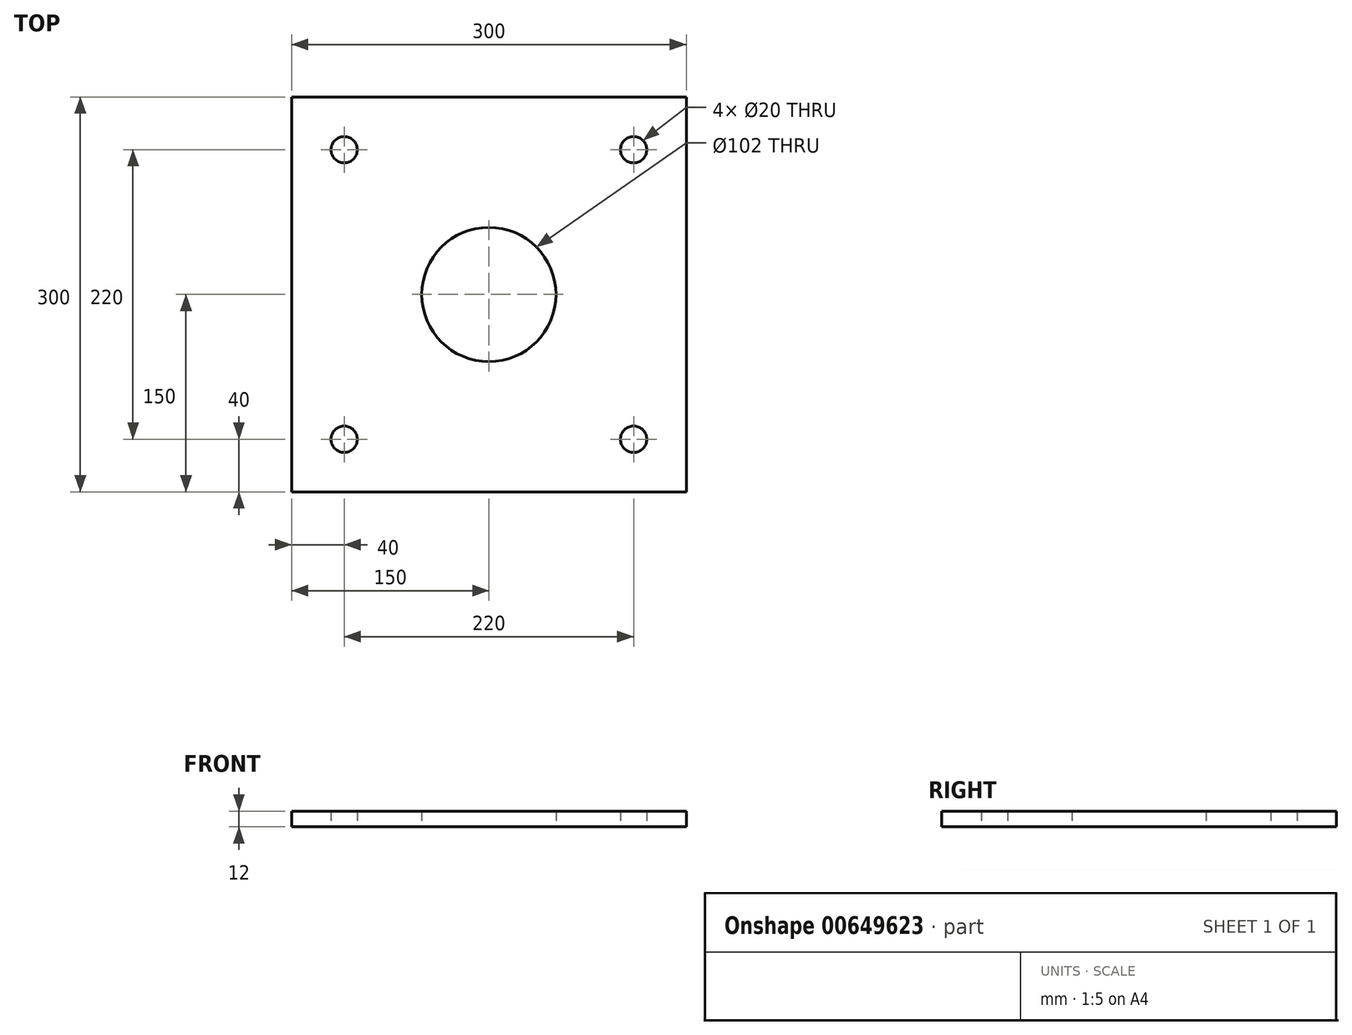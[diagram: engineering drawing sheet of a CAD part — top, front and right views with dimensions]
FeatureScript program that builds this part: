
annotation { "Feature Type Name" : "Feature", "Feature Type Description" : "" }
export const myFeature = defineFeature(function(context is Context, id is Id, definition is map)
    precondition{}
    {
        {
            var Q0;
            Q0=qCreatedBy(makeId("Top.planeOp"),FACE);
            var sketch = newSketch(context, id + "F0", { "sketchPlane" : qUnion([Q0])});
            skLineSegment(sketch, "E0.bottom", {"start": v(150, -150) * mm, "end": v(-150, -150) * mm});
            skLineSegment(sketch, "E0.top", {"start": v(150, 150) * mm, "end": v(-150, 150) * mm});
            skLineSegment(sketch, "E0.left", {"start": v(150, -150) * mm, "end": v(150, 150) * mm});
            skLineSegment(sketch, "E0.right", {"start": v(-150, -150) * mm, "end": v(-150, 150) * mm});
            skPoint(sketch, "E0.middle", {"position": v(0, 0) * mm});
            skCircle(sketch, "E1", {"center": v(0, 0) * mm, "radius": 51 * mm});
            skCircle(sketch, "E2", {"center": v(110, 110) * mm, "radius": 10 * mm});
            skCircle(sketch, "E3", {"center": v(110, -110) * mm, "radius": 10 * mm});
            skCircle(sketch, "E4", {"center": v(-110, -110) * mm, "radius": 10 * mm});
            skCircle(sketch, "E5", {"center": v(-110, 110) * mm, "radius": 10 * mm});
            skSolve(sketch);
        }
        {
            var Q0;
            Q0 = qSketchRegion(id + "F0", true);
            extrude(context, id + "F1", {"entities" : qUnion([Q0]), "depth" : 12 * mm, "offsetDistance" : 25 * mm});
        }
    });
